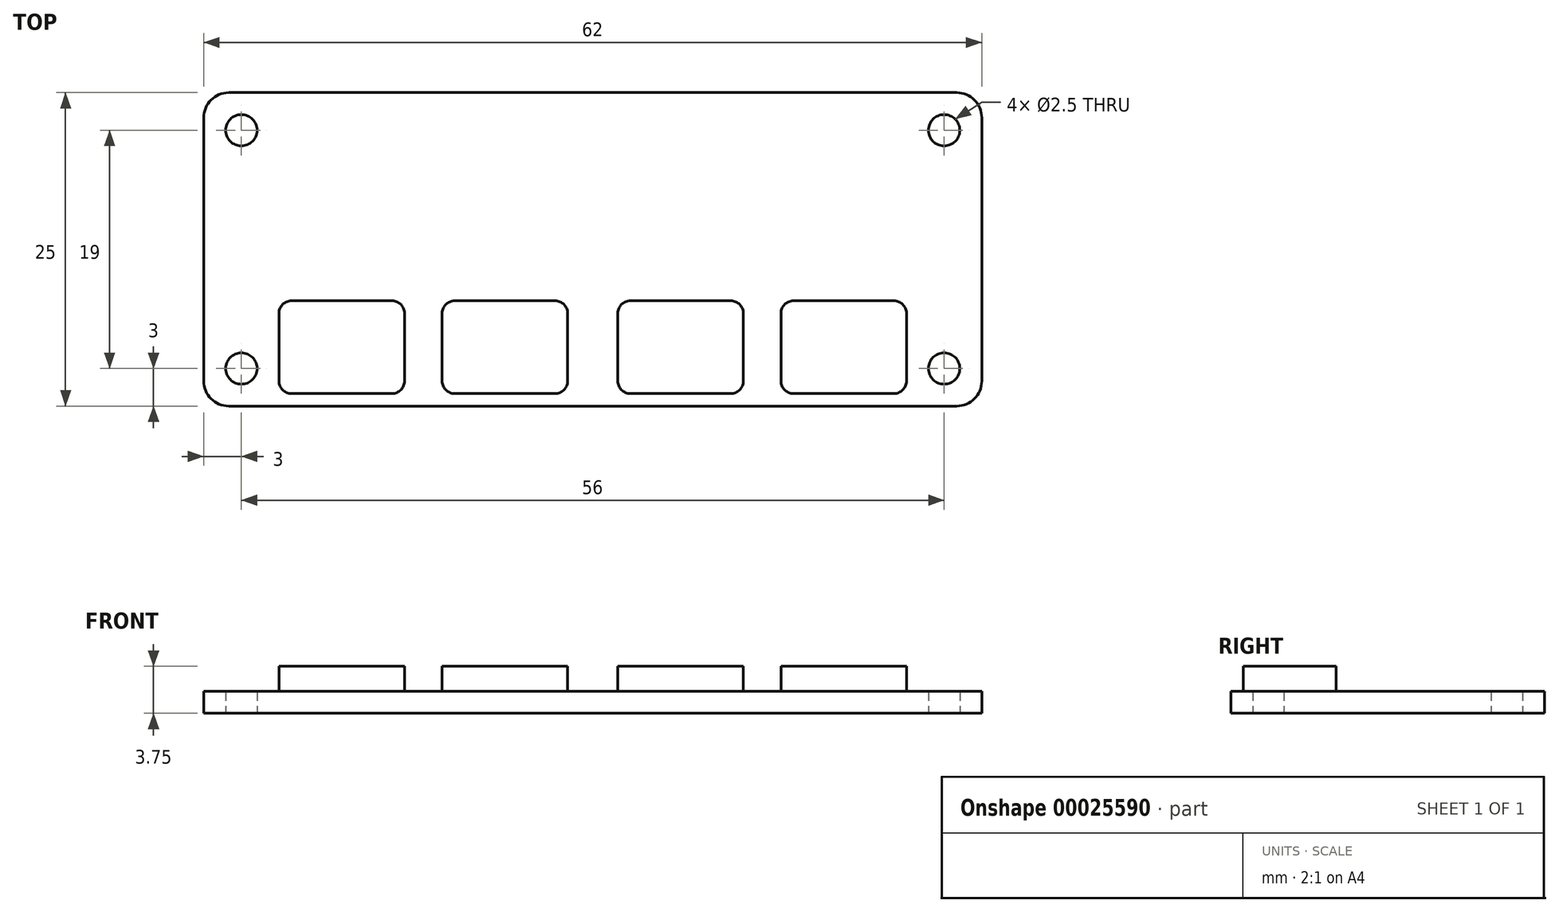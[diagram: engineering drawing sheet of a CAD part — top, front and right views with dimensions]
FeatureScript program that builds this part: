
annotation { "Feature Type Name" : "Feature", "Feature Type Description" : "" }
export const myFeature = defineFeature(function(context is Context, id is Id, definition is map)
    precondition{}
    {
        {
            var Q0;
            Q0=qCreatedBy(makeId("Top.planeOp"),FACE);
            var sketch = newSketch(context, id + "F0", { "sketchPlane" : qUnion([Q0])});
            skLineSegment(sketch, "E0.bottom", {"start": v(2, 0) * mm, "end": v(60, 0) * mm});
            skLineSegment(sketch, "E0.top", {"start": v(2, 25) * mm, "end": v(60, 25) * mm});
            skLineSegment(sketch, "E0.left", {"start": v(0, 2) * mm, "end": v(0, 23) * mm});
            skLineSegment(sketch, "E0.right", {"start": v(62, 2) * mm, "end": v(62, 23) * mm});
            skPoint(sketch, "E1.visualSharp", {"position": v(0, 25) * mm});
            skArc(sketch, "E1.filletArc", {"start": v(2, 25) * mm, "mid": v(0.59, 24.41) * mm, "end": v(0, 23) * mm});
            skPoint(sketch, "E2.visualSharp", {"position": v(0, 0) * mm});
            skArc(sketch, "E2.filletArc", {"start": v(0, 2) * mm, "mid": v(0.59, 0.59) * mm, "end": v(2, 0) * mm});
            skPoint(sketch, "E3.visualSharp", {"position": v(62, 0) * mm});
            skArc(sketch, "E3.filletArc", {"start": v(60, 0) * mm, "mid": v(61.41, 0.59) * mm, "end": v(62, 2) * mm});
            skPoint(sketch, "E4.visualSharp", {"position": v(62, 25) * mm});
            skArc(sketch, "E4.filletArc", {"start": v(62, 23) * mm, "mid": v(61.41, 24.41) * mm, "end": v(60, 25) * mm});
            skLineSegment(sketch, "E5", {"start": v(0, 22) * mm, "end": v(62, 22) * mm, "construction": true});
            skLineSegment(sketch, "E6", {"start": v(59, 25) * mm, "end": v(59, 0) * mm, "construction": true});
            skLineSegment(sketch, "E7", {"start": v(0, 3) * mm, "end": v(62, 3) * mm, "construction": true});
            skLineSegment(sketch, "E8", {"start": v(3, 25) * mm, "end": v(3, 0) * mm, "construction": true});
            skCircle(sketch, "E9", {"center": v(3, 22) * mm, "radius": 1.25 * mm});
            skCircle(sketch, "E10", {"center": v(3, 3) * mm, "radius": 1.25 * mm});
            skCircle(sketch, "E11", {"center": v(59, 3) * mm, "radius": 1.25 * mm});
            skCircle(sketch, "E12", {"center": v(59, 22) * mm, "radius": 1.25 * mm});
            skSolve(sketch);
        }
        {
            var Q0;
            Q0=makeQuery(id+"F0.imprint","IMPRINT",FACE,{"disambiguationData":[TD([[makeQuery(id+"F0.imprint","IMPRINT",EDGE,{"derivedFrom":sQuery(id+"F0.wireOp",EDGE,"E0.bottom")}),1.0]])]});
            extrude(context, id + "F1", {"entities" : qUnion([Q0]), "depth" : 1.75 * mm});
        }
        {
            var Q0;
            Q0=makeQuery(id+"F1.opExtrude","CAP_FACE",FACE,{"disambiguationData":[OSD([sQuery(id+"F0.wireOp",EDGE,"E0.bottom"),sQuery(id+"F0.wireOp",EDGE,"E0.top"),sQuery(id+"F0.wireOp",EDGE,"E0.left"),sQuery(id+"F0.wireOp",EDGE,"E0.right"),sQuery(id+"F0.wireOp",EDGE,"E1.filletArc"),sQuery(id+"F0.wireOp",EDGE,"E2.filletArc"),sQuery(id+"F0.wireOp",EDGE,"E3.filletArc"),sQuery(id+"F0.wireOp",EDGE,"E4.filletArc"),sQuery(id+"F0.wireOp",EDGE,"E9"),sQuery(id+"F0.wireOp",EDGE,"E10"),sQuery(id+"F0.wireOp",EDGE,"E11"),sQuery(id+"F0.wireOp",EDGE,"E12")])],"isStart":false});
            var sketch = newSketch(context, id + "F2", { "sketchPlane" : qUnion([Q0])});
            skLineSegment(sketch, "E13", {"start": v(0, 8.4) * mm, "end": v(62, 8.4) * mm, "construction": true});
            skLineSegment(sketch, "E14", {"start": v(0, 1) * mm, "end": v(62, 1) * mm, "construction": true});
            skLineSegment(sketch, "E15.bottom", {"start": v(6, 1) * mm, "end": v(16, 1) * mm});
            skLineSegment(sketch, "E15.top", {"start": v(6, 8.4) * mm, "end": v(16, 8.4) * mm});
            skLineSegment(sketch, "E15.left", {"start": v(6, 1) * mm, "end": v(6, 8.4) * mm});
            skLineSegment(sketch, "E15.right", {"start": v(16, 1) * mm, "end": v(16, 8.4) * mm});
            skLineSegment(sketch, "E16.bottom", {"start": v(19, 1) * mm, "end": v(29, 1) * mm});
            skLineSegment(sketch, "E16.top", {"start": v(19, 8.4) * mm, "end": v(29, 8.4) * mm});
            skLineSegment(sketch, "E16.left", {"start": v(19, 1) * mm, "end": v(19, 8.4) * mm});
            skLineSegment(sketch, "E16.right", {"start": v(29, 1) * mm, "end": v(29, 8.4) * mm});
            skLineSegment(sketch, "E17.bottom", {"start": v(33, 8.4) * mm, "end": v(43, 8.4) * mm});
            skLineSegment(sketch, "E17.top", {"start": v(33, 1) * mm, "end": v(43, 1) * mm});
            skLineSegment(sketch, "E17.left", {"start": v(33, 8.4) * mm, "end": v(33, 1) * mm});
            skLineSegment(sketch, "E17.right", {"start": v(43, 8.4) * mm, "end": v(43, 1) * mm});
            skLineSegment(sketch, "E18.bottom", {"start": v(46, 8.4) * mm, "end": v(56, 8.4) * mm});
            skLineSegment(sketch, "E18.top", {"start": v(46, 1) * mm, "end": v(56, 1) * mm});
            skLineSegment(sketch, "E18.left", {"start": v(46, 8.4) * mm, "end": v(46, 1) * mm});
            skLineSegment(sketch, "E18.right", {"start": v(56, 8.4) * mm, "end": v(56, 1) * mm});
            skSolve(sketch);
        }
        {
            var Q0;
            Q0 = qSketchRegion(id + "F2", true);
            extrude(context, id + "F3", {"entities" : qUnion([Q0]), "depth" : 2 * mm});
        }
        {
            var Q0;
            Q0=makeQuery(id+"F3.opExtrude","SWEPT_EDGE",EDGE,{"disambiguationData":[OSD([sQuery(id+"F2.wireOp",EDGE,"E15.bottom"),sQuery(id+"F2.wireOp",EDGE,"E15.left")])]});
            var Q1;
            Q1=makeQuery(id+"F3.opExtrude","SWEPT_EDGE",EDGE,{"disambiguationData":[OSD([sQuery(id+"F2.wireOp",EDGE,"E15.top"),sQuery(id+"F2.wireOp",EDGE,"E15.left")])]});
            var Q2;
            Q2=makeQuery(id+"F3.opExtrude","SWEPT_EDGE",EDGE,{"disambiguationData":[OSD([sQuery(id+"F2.wireOp",EDGE,"E15.top"),sQuery(id+"F2.wireOp",EDGE,"E15.right")])]});
            var Q3;
            Q3=makeQuery(id+"F3.opExtrude","SWEPT_EDGE",EDGE,{"disambiguationData":[OSD([sQuery(id+"F2.wireOp",EDGE,"E16.top"),sQuery(id+"F2.wireOp",EDGE,"E16.left")])]});
            var Q4;
            Q4=makeQuery(id+"F3.opExtrude","SWEPT_EDGE",EDGE,{"disambiguationData":[OSD([sQuery(id+"F2.wireOp",EDGE,"E16.bottom"),sQuery(id+"F2.wireOp",EDGE,"E16.left")])]});
            var Q5;
            Q5=makeQuery(id+"F3.opExtrude","SWEPT_EDGE",EDGE,{"disambiguationData":[OSD([sQuery(id+"F2.wireOp",EDGE,"E17.top"),sQuery(id+"F2.wireOp",EDGE,"E17.left")])]});
            var Q6;
            Q6=makeQuery(id+"F3.opExtrude","SWEPT_EDGE",EDGE,{"disambiguationData":[OSD([sQuery(id+"F2.wireOp",EDGE,"E17.bottom"),sQuery(id+"F2.wireOp",EDGE,"E17.left")])]});
            var Q7;
            Q7=makeQuery(id+"F3.opExtrude","SWEPT_EDGE",EDGE,{"disambiguationData":[OSD([sQuery(id+"F2.wireOp",EDGE,"E16.top"),sQuery(id+"F2.wireOp",EDGE,"E16.right")])]});
            var Q8;
            Q8=makeQuery(id+"F3.opExtrude","SWEPT_EDGE",EDGE,{"disambiguationData":[OSD([sQuery(id+"F2.wireOp",EDGE,"E18.bottom"),sQuery(id+"F2.wireOp",EDGE,"E18.left")])]});
            var Q9;
            Q9=makeQuery(id+"F3.opExtrude","SWEPT_EDGE",EDGE,{"disambiguationData":[OSD([sQuery(id+"F2.wireOp",EDGE,"E17.bottom"),sQuery(id+"F2.wireOp",EDGE,"E17.right")])]});
            var Q10;
            Q10=makeQuery(id+"F3.opExtrude","SWEPT_EDGE",EDGE,{"disambiguationData":[OSD([sQuery(id+"F2.wireOp",EDGE,"E18.top"),sQuery(id+"F2.wireOp",EDGE,"E18.left")])]});
            var Q11;
            Q11=makeQuery(id+"F3.opExtrude","SWEPT_EDGE",EDGE,{"disambiguationData":[OSD([sQuery(id+"F2.wireOp",EDGE,"E18.bottom"),sQuery(id+"F2.wireOp",EDGE,"E18.right")])]});
            var Q12;
            Q12=makeQuery(id+"F3.opExtrude","SWEPT_EDGE",EDGE,{"disambiguationData":[OSD([sQuery(id+"F2.wireOp",EDGE,"E18.top"),sQuery(id+"F2.wireOp",EDGE,"E18.right")])]});
            var Q13;
            Q13=makeQuery(id+"F3.opExtrude","SWEPT_EDGE",EDGE,{"disambiguationData":[OSD([sQuery(id+"F2.wireOp",EDGE,"E16.bottom"),sQuery(id+"F2.wireOp",EDGE,"E16.right")])]});
            var Q14;
            Q14=makeQuery(id+"F3.opExtrude","SWEPT_EDGE",EDGE,{"disambiguationData":[OSD([sQuery(id+"F2.wireOp",EDGE,"E15.bottom"),sQuery(id+"F2.wireOp",EDGE,"E15.right")])]});
            var Q15;
            Q15=makeQuery(id+"F3.opExtrude","SWEPT_EDGE",EDGE,{"disambiguationData":[OSD([sQuery(id+"F2.wireOp",EDGE,"E17.top"),sQuery(id+"F2.wireOp",EDGE,"E17.right")])]});
            fillet(context, id + "F4", {"entities" : qUnion([Q0, Q1, Q2, Q3, Q4, Q5, Q6, Q7, Q8, Q9, Q10, Q11, Q12, Q13, Q14, Q15]), "radius" : 1 * mm, "tangentPropagation" : true, "allowEdgeOverflow" : false});
        }
    });
